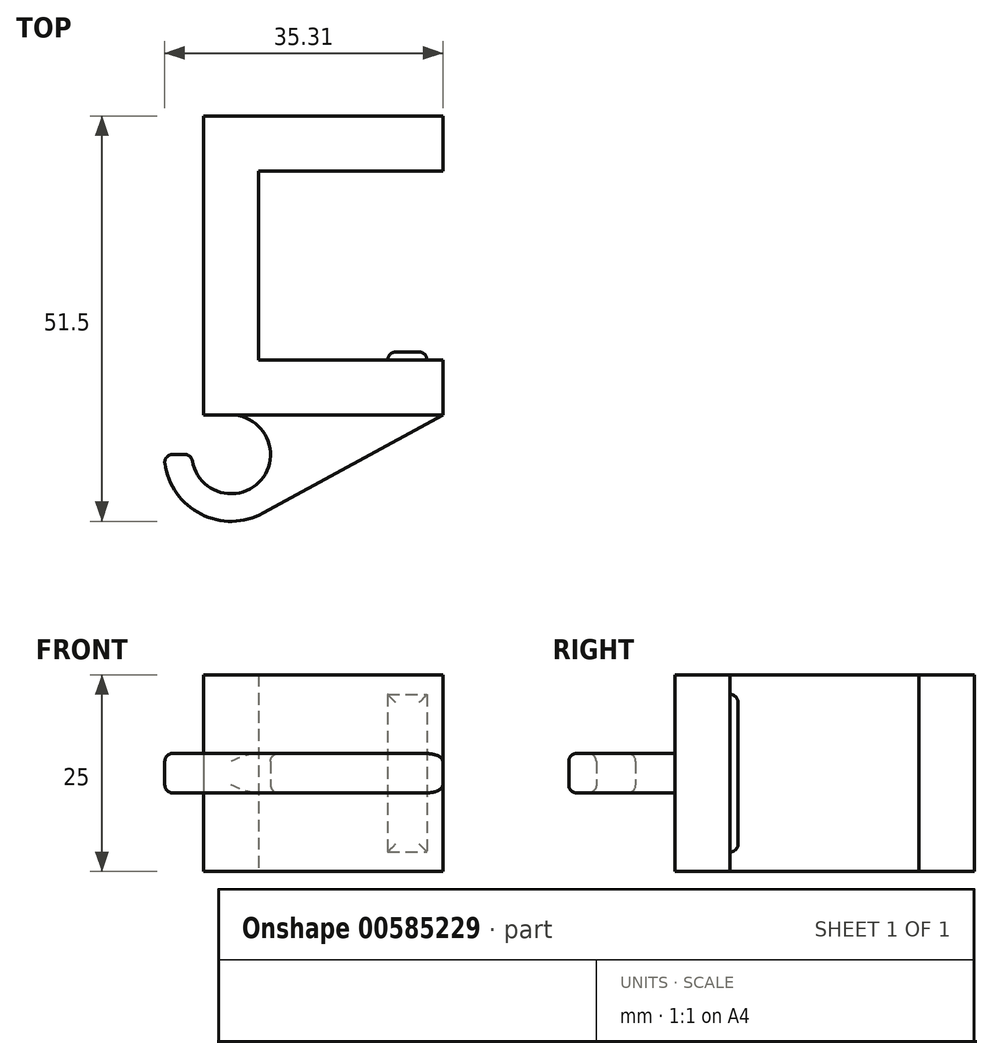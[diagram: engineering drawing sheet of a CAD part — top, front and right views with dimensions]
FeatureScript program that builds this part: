
annotation { "Feature Type Name" : "Feature", "Feature Type Description" : "" }
export const myFeature = defineFeature(function(context is Context, id is Id, definition is map)
    precondition{}
    {
        {
            var Q0;
            Q0=qCreatedBy(makeId("Top.planeOp"),FACE);
            var sketch = newSketch(context, id + "F0", { "sketchPlane" : qUnion([Q0])});
            skLineSegment(sketch, "E0", {"start": v(0, 0) * mm, "end": v(-23.38, 0) * mm});
            skLineSegment(sketch, "E1", {"start": v(-23.38, 0) * mm, "end": v(-23.38, -24) * mm});
            skLineSegment(sketch, "E2", {"start": v(-23.38, -24) * mm, "end": v(0, -24) * mm});
            skLineSegment(sketch, "E3", {"start": v(0, -24) * mm, "end": v(0, -31) * mm});
            skLineSegment(sketch, "E4", {"start": v(0, -31) * mm, "end": v(-30.38, -31) * mm});
            skLineSegment(sketch, "E5", {"start": v(-30.38, -31) * mm, "end": v(-30.38, 7) * mm});
            skLineSegment(sketch, "E6", {"start": v(-30.38, 7) * mm, "end": v(0, 7) * mm});
            skLineSegment(sketch, "E7", {"start": v(0, 7) * mm, "end": v(0, 0) * mm});
            skLineSegment(sketch, "E8", {"start": v(-2, -24) * mm, "end": v(-2, -23) * mm});
            skLineSegment(sketch, "E9", {"start": v(-2, -23) * mm, "end": v(-7, -23) * mm});
            skLineSegment(sketch, "E10", {"start": v(-7, -23) * mm, "end": v(-7, -24) * mm});
            skPoint(sketch, "E11", {"position": v(-26.88, -36) * mm});
            skLineSegment(sketch, "E12", {"start": v(0, -31) * mm, "end": v(-22.8, -43.46) * mm});
            skLineSegment(sketch, "E13", {"start": v(-26.88, -36) * mm, "end": v(-31.88, -36) * mm});
            skLineSegment(sketch, "E14", {"start": v(-31.88, -36) * mm, "end": v(-35.38, -36) * mm});
            skArc(sketch, "E15", {"start": v(-20, -31) * mm, "mid": v(-24.7, -27.78) * mm, "end": v(-30.38, -28.25) * mm});
            skLineSegment(sketch, "E16", {"start": v(-30.38, -28.25) * mm, "end": v(-30.38, -28.25) * mm});
            skArc(sketch, "E17", {"start": v(-26.88, -31) * mm, "mid": v(-30.42, -32.46) * mm, "end": v(-31.88, -36) * mm});
            skArc(sketch, "E18", {"start": v(-31.88, -36) * mm, "mid": v(-23.34, -39.54) * mm, "end": v(-26.88, -31) * mm});
            skArc(sketch, "E19", {"start": v(-30.38, -28.25) * mm, "mid": v(-34.02, -31.4) * mm, "end": v(-35.38, -36) * mm});
            skArc(sketch, "E20", {"start": v(-35.38, -36) * mm, "mid": v(-24.25, -44.08) * mm, "end": v(-20, -31) * mm});
            skSolve(sketch);
        }
        {
            var Q0;
            Q0=makeQuery(id+"F0.imprint","IMPRINT",FACE,{"disambiguationData":[TD([[makeQuery(id+"F0.imprint","IMPRINT",EDGE,{"derivedFrom":sQuery(id+"F0.wireOp",EDGE,"E0")}),-1.0]])]});
            var Q1;
            {var subQ0=sQuery(id+"F0.wireOp",EDGE,"E15");Q1=makeQuery(id+"F0.imprint","IMPRINT",FACE,{"disambiguationData":[TD([[makeQuery(id+"F0.imprint","IMPRINT",EDGE,{"derivedFrom":subQ0}),1.0]])]});}
            extrude(context, id + "F1", {"entities" : qUnion([Q0, Q1]), "endBound" : BoundingType.SYMMETRIC, "depth" : 25 * mm, "offsetDistance" : 25 * mm});
        }
        {
            var Q0;
            {var subQ0=sQuery(id+"F0.wireOp",EDGE,"E8");Q0=makeQuery(id+"F0.imprint","IMPRINT",FACE,{"disambiguationData":[TD([[makeQuery(id+"F0.imprint","IMPRINT",EDGE,{"derivedFrom":subQ0}),1.0]])]});}
            extrude(context, id + "F2", {"entities" : qUnion([Q0]), "operationType" : NewBodyOperationType.ADD, "endBound" : BoundingType.SYMMETRIC, "depth" : 20 * mm, "offsetDistance" : 25 * mm});
        }
        {
            var Q0;
            {var subQ3=sQuery(id+"F0.wireOp",EDGE,"E14");Q0=makeQuery(id+"F0.imprint","IMPRINT",FACE,{"disambiguationData":[TD([[makeQuery(id+"F0.imprint","IMPRINT",EDGE,{"derivedFrom":subQ3}),1.0]])]});}
            var Q1;
            {var subQ0=sQuery(id+"F0.wireOp",EDGE,"E12");Q1=makeQuery(id+"F0.imprint","IMPRINT",FACE,{"disambiguationData":[TD([[makeQuery(id+"F0.imprint","IMPRINT",EDGE,{"derivedFrom":subQ0}),-1.0]])]});}
            extrude(context, id + "F3", {"entities" : qUnion([Q0, Q1]), "operationType" : NewBodyOperationType.ADD, "endBound" : BoundingType.SYMMETRIC, "depth" : 5 * mm, "offsetDistance" : 25 * mm});
        }
        {
            var Q0;
            Q0=makeQuery(id+"F2.opExtrude","CAP_EDGE",EDGE,{"disambiguationData":[OSD([sQuery(id+"F0.wireOp",EDGE,"E9")])],"isStart":false});
            var Q1;
            Q1=makeQuery(id+"F2.opExtrude","SWEPT_EDGE",EDGE,{"disambiguationData":[OSD([sQuery(id+"F0.wireOp",EDGE,"E9"),sQuery(id+"F0.wireOp",EDGE,"E10")])]});
            var Q2;
            Q2=makeQuery(id+"F2.opExtrude","SWEPT_EDGE",EDGE,{"disambiguationData":[OSD([sQuery(id+"F0.wireOp",EDGE,"E8"),sQuery(id+"F0.wireOp",EDGE,"E9")])]});
            var Q3;
            Q3=makeQuery(id+"F2.opExtrude","CAP_EDGE",EDGE,{"disambiguationData":[OSD([sQuery(id+"F0.wireOp",EDGE,"E9")])],"isStart":true});
            fillet(context, id + "F4", {"entities" : qUnion([Q0, Q1, Q2, Q3]), "radius" : 1 * mm, "tangentPropagation" : true, "allowEdgeOverflow" : false});
        }
        {
            var Q0;
            Q0=makeQuery(id+"F3.opExtrude","CAP_EDGE",EDGE,{"disambiguationData":[OSD([sQuery(id+"F0.wireOp",EDGE,"E18")])],"isStart":false});
            var Q1;
            Q1=makeQuery(id+"F3.opExtrude","CAP_EDGE",EDGE,{"disambiguationData":[OSD([sQuery(id+"F0.wireOp",EDGE,"E18")])],"isStart":true});
            var Q2;
            Q2=makeQuery(id+"F3.opExtrude","CAP_EDGE",EDGE,{"disambiguationData":[OSD([sQuery(id+"F0.wireOp",EDGE,"E20")])],"isStart":false});
            var Q3;
            Q3=makeQuery(id+"F3.opExtrude","CAP_EDGE",EDGE,{"disambiguationData":[OSD([sQuery(id+"F0.wireOp",EDGE,"E20")])],"isStart":true});
            var Q4;
            Q4=makeQuery(id+"F3.opExtrude","SWEPT_EDGE",EDGE,{"disambiguationData":[OSD([sQuery(id+"F0.wireOp",EDGE,"E14"),sQuery(id+"F0.wireOp",EDGE,"E17"),sQuery(id+"F0.wireOp",EDGE,"E18")])]});
            var Q5;
            Q5=makeQuery(id+"F3.opExtrude","SWEPT_EDGE",EDGE,{"disambiguationData":[OSD([sQuery(id+"F0.wireOp",EDGE,"E14"),sQuery(id+"F0.wireOp",EDGE,"E19"),sQuery(id+"F0.wireOp",EDGE,"E20")])]});
            var Q6;
            Q6=makeQuery(id+"F3.opExtrude","CAP_EDGE",EDGE,{"disambiguationData":[OSD([sQuery(id+"F0.wireOp",EDGE,"E14")])],"isStart":false});
            var Q7;
            Q7=makeQuery(id+"F3.opExtrude","CAP_EDGE",EDGE,{"disambiguationData":[OSD([sQuery(id+"F0.wireOp",EDGE,"E14")])],"isStart":true});
            fillet(context, id + "F5", {"entities" : qUnion([Q0, Q1, Q2, Q3, Q4, Q5, Q6, Q7]), "radius" : 1 * mm, "tangentPropagation" : true, "allowEdgeOverflow" : false});
        }
    });
